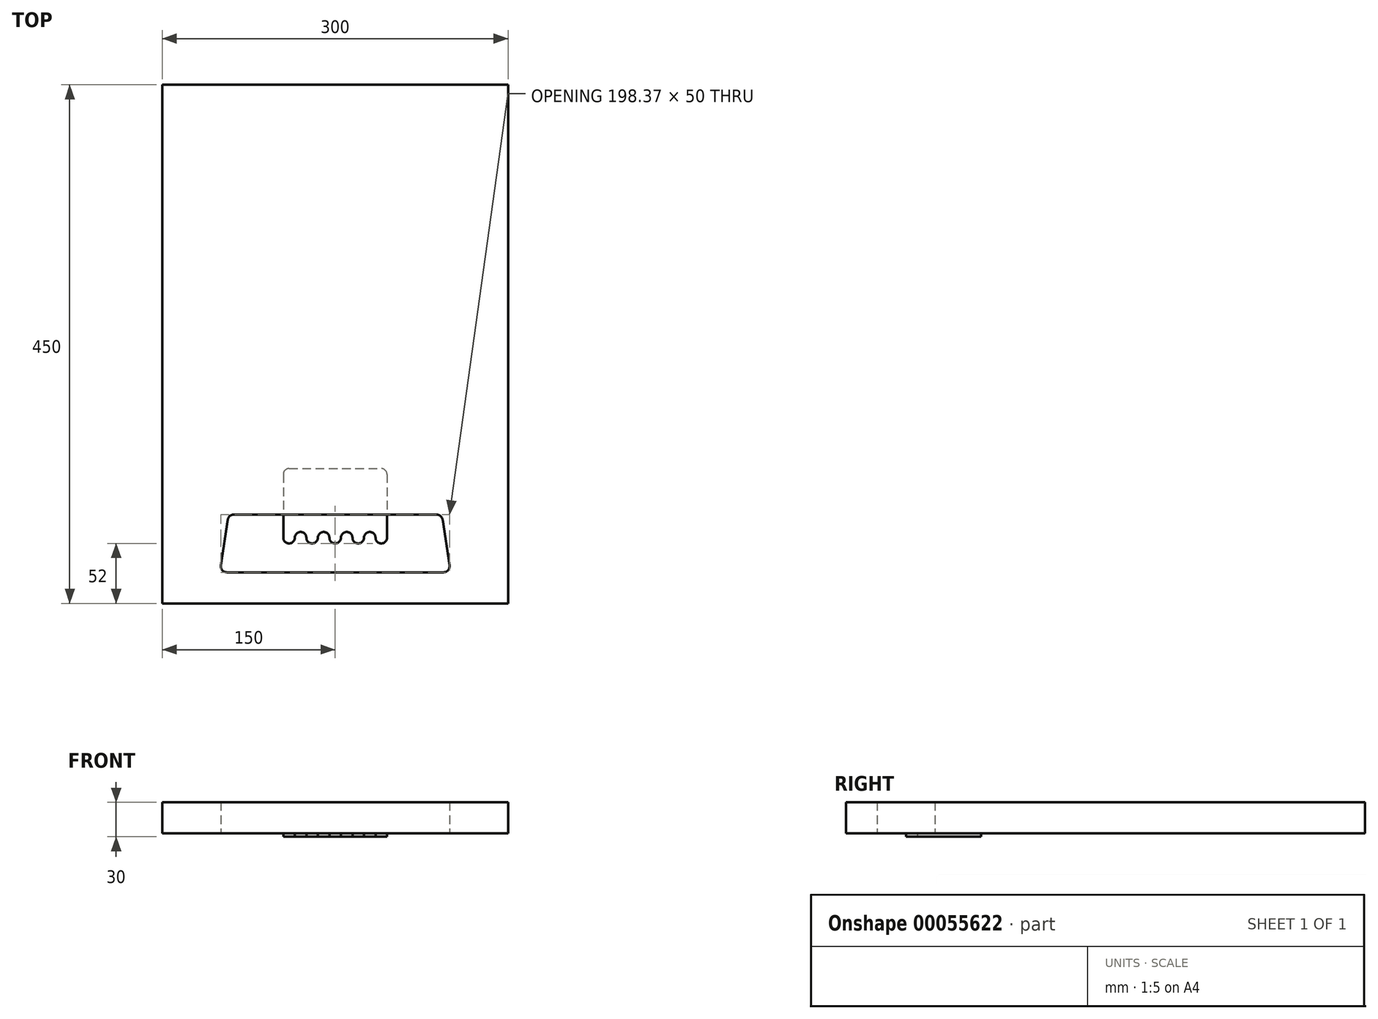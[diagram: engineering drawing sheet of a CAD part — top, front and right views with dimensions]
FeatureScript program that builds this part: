
annotation { "Feature Type Name" : "Feature", "Feature Type Description" : "" }
export const myFeature = defineFeature(function(context is Context, id is Id, definition is map)
    precondition{}
    {
        {
            var Q0;
            Q0=qCreatedBy(makeId("Top.planeOp"),FACE);
            var sketch = newSketch(context, id + "F0", { "sketchPlane" : qUnion([Q0])});
            skLineSegment(sketch, "E0.bottom", {"start": v(-150, 0) * mm, "end": v(150, 0) * mm});
            skLineSegment(sketch, "E0.top", {"start": v(-150, 450) * mm, "end": v(150, 450) * mm});
            skLineSegment(sketch, "E0.left", {"start": v(-150, 0) * mm, "end": v(-150, 450) * mm});
            skLineSegment(sketch, "E0.right", {"start": v(150, 0) * mm, "end": v(150, 450) * mm});
            skLineSegment(sketch, "E1", {"start": v(-94.2, 27) * mm, "end": v(0, 27) * mm});
            skLineSegment(sketch, "E2", {"start": v(-93.14, 72.74) * mm, "end": v(-99.14, 32.74) * mm});
            skLineSegment(sketch, "E3", {"start": v(0, 0) * mm, "end": v(0, 450) * mm, "construction": true});
            skPoint(sketch, "E4", {"position": v(0, 27) * mm});
            skLineSegment(sketch, "E5", {"start": v(-88.2, 77) * mm, "end": v(0, 77) * mm});
            skPoint(sketch, "E6.visualSharp", {"position": v(-92.5, 77) * mm});
            skArc(sketch, "E6.filletArc", {"start": v(-88.2, 77) * mm, "mid": v(-91.46, 75.79) * mm, "end": v(-93.14, 72.74) * mm});
            skPoint(sketch, "E7.visualSharp", {"position": v(-100, 27) * mm});
            skArc(sketch, "E7.filletArc", {"start": v(-99.14, 32.74) * mm, "mid": v(-97.98, 28.74) * mm, "end": v(-94.2, 27) * mm});
            skLineSegment(sketch, "E8.MirrorCS", {"start": v(88.2, 77) * mm, "end": v(0, 77) * mm});
            skArc(sketch, "E9.MirrorCS", {"start": v(88.2, 77) * mm, "mid": v(91.46, 75.79) * mm, "end": v(93.14, 72.74) * mm});
            skLineSegment(sketch, "E10.MirrorCS", {"start": v(93.14, 72.74) * mm, "end": v(99.14, 32.74) * mm});
            skArc(sketch, "E11.MirrorCS", {"start": v(99.14, 32.74) * mm, "mid": v(97.98, 28.74) * mm, "end": v(94.2, 27) * mm});
            skLineSegment(sketch, "E12.MirrorCS", {"start": v(94.2, 27) * mm, "end": v(0, 27) * mm});
            skLineSegment(sketch, "E13", {"start": v(0, 117) * mm, "end": v(-40, 117) * mm});
            skLineSegment(sketch, "E14", {"start": v(-45, 112) * mm, "end": v(-45, 57) * mm});
            skArc(sketch, "E15", {"start": v(-45, 57) * mm, "mid": v(-40, 52) * mm, "end": v(-35, 57) * mm});
            skArc(sketch, "E16", {"start": v(-35, 57) * mm, "mid": v(-30, 62) * mm, "end": v(-25, 57) * mm});
            skArc(sketch, "E17", {"start": v(-25, 57) * mm, "mid": v(-20, 52) * mm, "end": v(-15, 57) * mm});
            skArc(sketch, "E18", {"start": v(-15, 57) * mm, "mid": v(-10, 62) * mm, "end": v(-5, 57) * mm});
            skArc(sketch, "E19", {"start": v(-5, 57) * mm, "mid": v(-3.54, 53.46) * mm, "end": v(0, 52) * mm});
            skPoint(sketch, "E20.orphan", {"position": v(5, 57) * mm});
            skLineSegment(sketch, "E21.MirrorCS", {"start": v(0, 117) * mm, "end": v(40, 117) * mm});
            skLineSegment(sketch, "E22.MirrorCS", {"start": v(45, 112) * mm, "end": v(45, 57) * mm});
            skArc(sketch, "E23.MirrorCS", {"start": v(45, 57) * mm, "mid": v(40, 52) * mm, "end": v(35, 57) * mm});
            skArc(sketch, "E24.MirrorCS", {"start": v(35, 57) * mm, "mid": v(30, 62) * mm, "end": v(25, 57) * mm});
            skArc(sketch, "E25.MirrorCS", {"start": v(25, 57) * mm, "mid": v(20, 52) * mm, "end": v(15, 57) * mm});
            skArc(sketch, "E26.MirrorCS", {"start": v(15, 57) * mm, "mid": v(10, 62) * mm, "end": v(5, 57) * mm});
            skArc(sketch, "E27.MirrorCS", {"start": v(5, 57) * mm, "mid": v(3.54, 53.46) * mm, "end": v(0, 52) * mm});
            skPoint(sketch, "E28.visualSharp", {"position": v(45, 117) * mm});
            skArc(sketch, "E28.filletArc", {"start": v(45, 112) * mm, "mid": v(43.54, 115.54) * mm, "end": v(40, 117) * mm});
            skPoint(sketch, "E29.visualSharp", {"position": v(-45, 117) * mm});
            skArc(sketch, "E29.filletArc", {"start": v(-40, 117) * mm, "mid": v(-43.54, 115.54) * mm, "end": v(-45, 112) * mm});
            skSolve(sketch);
        }
        {
            var Q0;
            {var subQ1=sQuery(id+"F0.wireOp",EDGE,"E13");Q0=makeQuery(id+"F0.imprint","IMPRINT",FACE,{"disambiguationData":[TD([[makeQuery(id+"F0.imprint","IMPRINT",EDGE,{"derivedFrom":subQ1}),1.0]])]});}
            var Q1;
            Q1=makeQuery(id+"F0.imprint","IMPRINT",FACE,{"disambiguationData":[TD([[makeQuery(id+"F0.imprint","IMPRINT",EDGE,{"derivedFrom":sQuery(id+"F0.wireOp",EDGE,"E0.bottom")}),1.0]])]});
            extrude(context, id + "F1", {"entities" : qUnion([Q0, Q1]), "depth" : 27 * mm});
        }
        {
            var Q0;
            {var subQ6=sQuery(id+"F0.wireOp",EDGE,"E15");Q0=makeQuery(id+"F0.imprint","IMPRINT",FACE,{"disambiguationData":[TD([[makeQuery(id+"F0.imprint","IMPRINT",EDGE,{"derivedFrom":subQ6}),1.0]])]});}
            var Q1;
            {var subQ1=sQuery(id+"F0.wireOp",EDGE,"E13");Q1=makeQuery(id+"F0.imprint","IMPRINT",FACE,{"disambiguationData":[TD([[makeQuery(id+"F0.imprint","IMPRINT",EDGE,{"derivedFrom":subQ1}),1.0]])]});}
            extrude(context, id + "F2", {"entities" : qUnion([Q0, Q1]), "oppositeDirection" : true, "depth" : 3 * mm});
        }
    });
